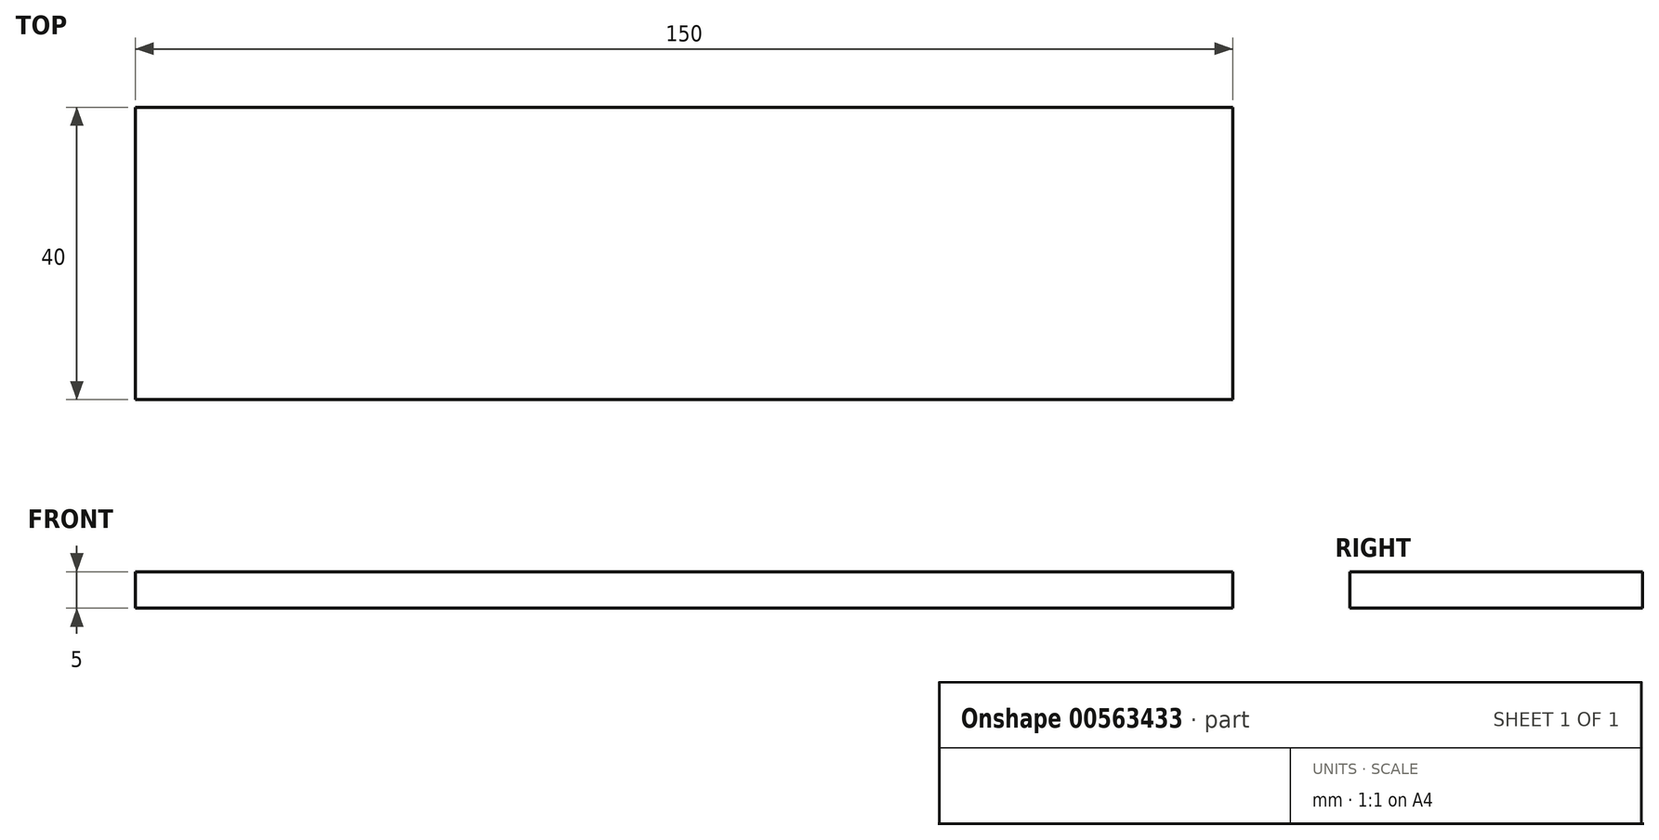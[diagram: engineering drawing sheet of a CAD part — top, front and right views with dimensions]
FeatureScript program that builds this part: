
annotation { "Feature Type Name" : "Feature", "Feature Type Description" : "" }
export const myFeature = defineFeature(function(context is Context, id is Id, definition is map)
    precondition{}
    {
        {
            var Q0;
            Q0=qCreatedBy(makeId("Top.planeOp"),FACE);
            var sketch = newSketch(context, id + "F0", { "sketchPlane" : qUnion([Q0])});
            skLineSegment(sketch, "E0.bottom", {"start": v(75, 20) * mm, "end": v(-75, 20) * mm});
            skLineSegment(sketch, "E0.top", {"start": v(75, -20) * mm, "end": v(-75, -20) * mm});
            skLineSegment(sketch, "E0.left", {"start": v(75, 20) * mm, "end": v(75, -20) * mm});
            skLineSegment(sketch, "E0.right", {"start": v(-75, 20) * mm, "end": v(-75, -20) * mm});
            skPoint(sketch, "E0.middle", {"position": v(0, 0) * mm});
            skSolve(sketch);
        }
        {
            var Q0;
            Q0=makeQuery(id+"F0.imprint","IMPRINT",FACE,{"disambiguationData":[TD([[makeQuery(id+"F0.imprint","IMPRINT",EDGE,{"derivedFrom":sQuery(id+"F0.wireOp",EDGE,"E0.bottom")}),1.0]])]});
            extrude(context, id + "F1", {"entities" : qUnion([Q0]), "depth" : 5 * mm, "offsetDistance" : 25.4 * mm});
        }
    });
